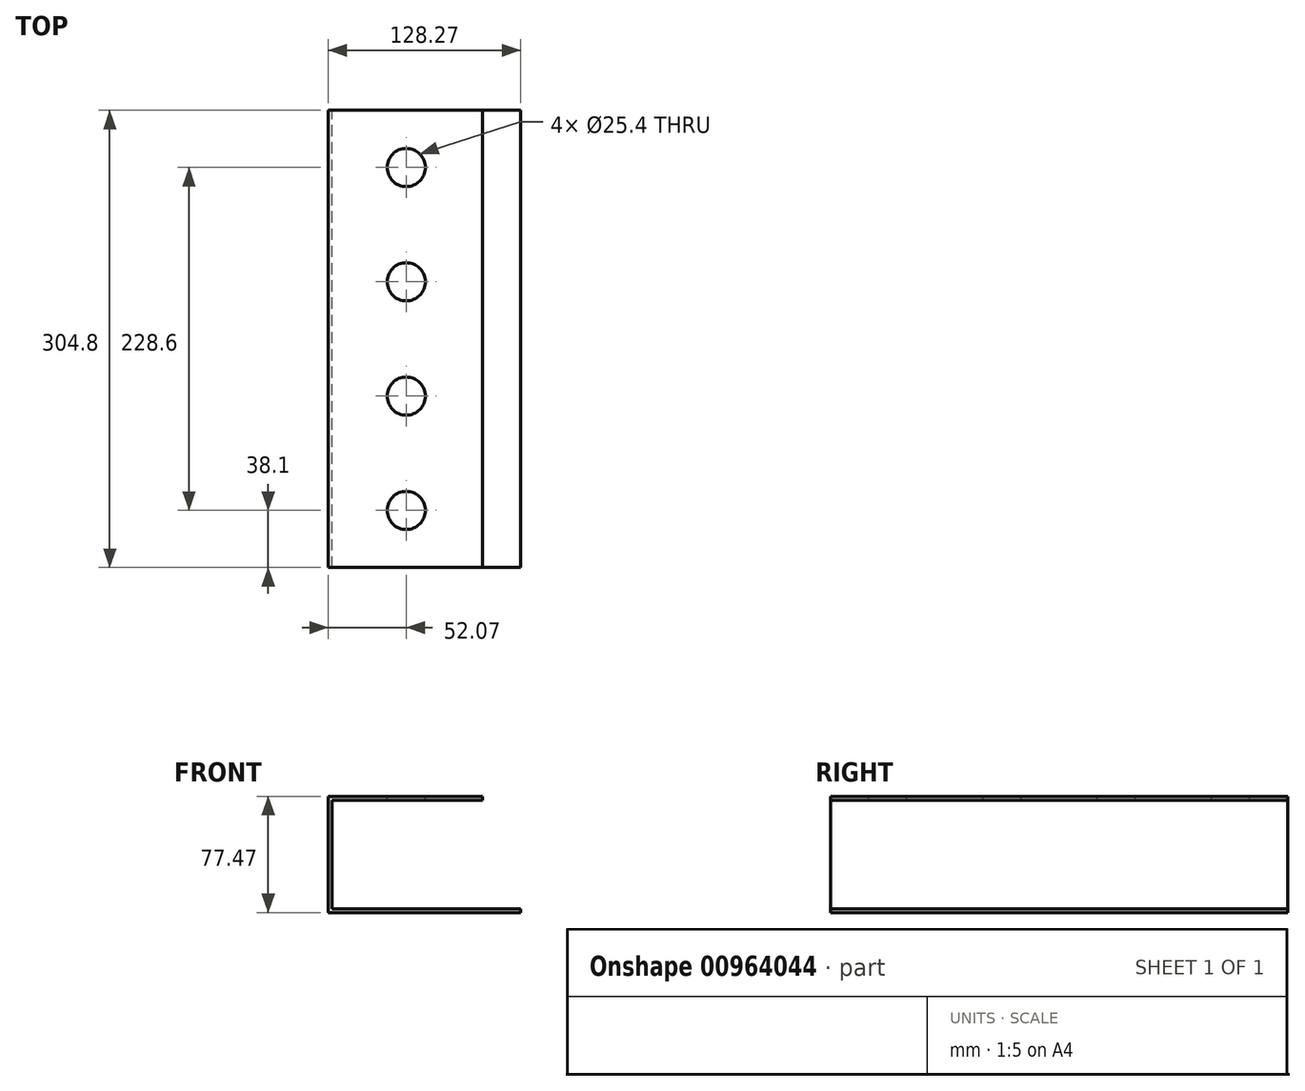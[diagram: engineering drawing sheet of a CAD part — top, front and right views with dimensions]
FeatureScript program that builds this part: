
annotation { "Feature Type Name" : "Feature", "Feature Type Description" : "" }
export const myFeature = defineFeature(function(context is Context, id is Id, definition is map)
    precondition{}
    {
        {
            var Q0;
            Q0=qCreatedBy(makeId("Front.planeOp"),FACE);
            var sketch = newSketch(context, id + "F0", { "sketchPlane" : qUnion([Q0])});
            skLineSegment(sketch, "E0", {"start": v(0, 0) * mm, "end": v(-128.27, 0) * mm});
            skLineSegment(sketch, "E1", {"start": v(-128.27, 0) * mm, "end": v(-128.27, 77.47) * mm});
            skLineSegment(sketch, "E2", {"start": v(-128.27, 77.47) * mm, "end": v(-25.4, 77.47) * mm});
            skLineSegment(sketch, "E3", {"start": v(-25.4, 77.47) * mm, "end": v(-25.4, 74.93) * mm});
            skLineSegment(sketch, "E4", {"start": v(-25.4, 74.93) * mm, "end": v(-125.73, 74.93) * mm});
            skLineSegment(sketch, "E5", {"start": v(-125.73, 74.93) * mm, "end": v(-125.73, 2.54) * mm});
            skLineSegment(sketch, "E6", {"start": v(-125.73, 2.54) * mm, "end": v(0, 2.54) * mm});
            skLineSegment(sketch, "E7", {"start": v(0, 2.54) * mm, "end": v(0, 0) * mm});
            skSolve(sketch);
        }
        {
            var Q0;
            Q0=makeQuery(id+"F0.imprint","IMPRINT",FACE,{"disambiguationData":[TD([[makeQuery(id+"F0.imprint","IMPRINT",EDGE,{"derivedFrom":sQuery(id+"F0.wireOp",EDGE,"E0")}),-1.0]])]});
            extrude(context, id + "F1", {"entities" : qUnion([Q0]), "depth" : 304.8 * mm, "offsetDistance" : 25.4 * mm});
        }
        {
            var Q0;
            Q0=makeQuery(id+"F1.opExtrude","SWEPT_FACE",FACE,{"disambiguationData":[OSD([sQuery(id+"F0.wireOp",EDGE,"E2")])]});
            var sketch = newSketch(context, id + "F2", { "sketchPlane" : qUnion([Q0])});
            skCircle(sketch, "E8", {"center": v(-76.2, -38.1) * mm, "radius": 12.7 * mm});
            skCircle(sketch, "E9", {"center": v(-76.2, -114.3) * mm, "radius": 12.7 * mm});
            skCircle(sketch, "E10", {"center": v(-76.2, -190.5) * mm, "radius": 12.7 * mm});
            skCircle(sketch, "E11", {"center": v(-76.2, -266.7) * mm, "radius": 12.7 * mm});
            skSolve(sketch);
        }
        {
            var Q0;
            Q0=makeQuery(id+"F2.imprint","IMPRINT",FACE,{"disambiguationData":[TD([[makeQuery(id+"F2.imprint","IMPRINT",EDGE,{"derivedFrom":sQuery(id+"F2.wireOp",EDGE,"E9")}),1.0]])]});
            var Q1;
            Q1=makeQuery(id+"F2.imprint","IMPRINT",FACE,{"disambiguationData":[TD([[makeQuery(id+"F2.imprint","IMPRINT",EDGE,{"derivedFrom":sQuery(id+"F2.wireOp",EDGE,"E11")}),1.0]])]});
            var Q2;
            Q2=makeQuery(id+"F2.imprint","IMPRINT",FACE,{"disambiguationData":[TD([[makeQuery(id+"F2.imprint","IMPRINT",EDGE,{"derivedFrom":sQuery(id+"F2.wireOp",EDGE,"E8")}),1.0]])]});
            var Q3;
            Q3=makeQuery(id+"F2.imprint","IMPRINT",FACE,{"disambiguationData":[TD([[makeQuery(id+"F2.imprint","IMPRINT",EDGE,{"derivedFrom":sQuery(id+"F2.wireOp",EDGE,"E10")}),1.0]])]});
            extrude(context, id + "F3", {"entities" : qUnion([Q0, Q1, Q2, Q3]), "operationType" : NewBodyOperationType.REMOVE, "oppositeDirection" : true, "depth" : 25.4 * mm, "offsetDistance" : 25.4 * mm});
        }
    });
